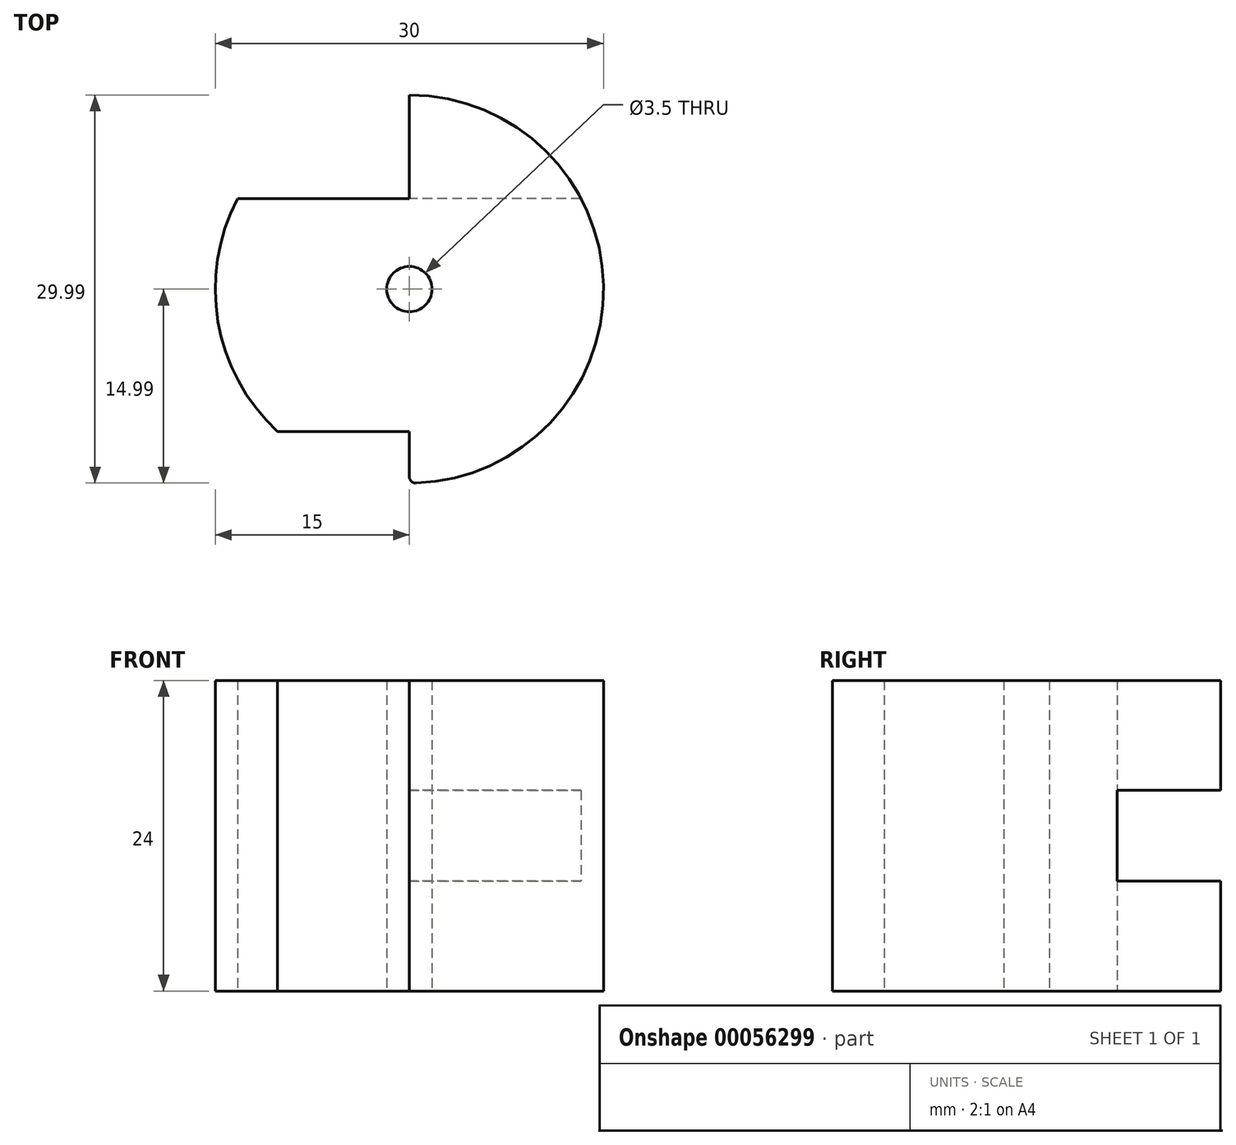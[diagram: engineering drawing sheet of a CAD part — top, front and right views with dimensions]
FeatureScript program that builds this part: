
annotation { "Feature Type Name" : "Feature", "Feature Type Description" : "" }
export const myFeature = defineFeature(function(context is Context, id is Id, definition is map)
    precondition{}
    {
        {
            var Q0;
            Q0=qCreatedBy(makeId("Top.planeOp"),FACE);
            var sketch = newSketch(context, id + "F0", { "sketchPlane" : qUnion([Q0])});
            skArc(sketch, "E0", {"start": v(-13.27, 7) * mm, "mid": v(-14.79, -2.52) * mm, "end": v(-10.2, -11) * mm});
            skLineSegment(sketch, "E1.bottom", {"start": v(-19.06, 20.86) * mm, "end": v(0, 20.86) * mm, "construction": true});
            skLineSegment(sketch, "E1.top", {"start": v(-19.06, 7) * mm, "end": v(-13.27, 7) * mm});
            skLineSegment(sketch, "E1.left", {"start": v(-19.06, 20.86) * mm, "end": v(-19.06, 7) * mm, "construction": true});
            skLineSegment(sketch, "E1.right", {"start": v(0, 20.86) * mm, "end": v(0, 7) * mm});
            skLineSegment(sketch, "E2.bottom", {"start": v(-16.2, -11) * mm, "end": v(-10.2, -11) * mm});
            skLineSegment(sketch, "E2.top", {"start": v(-16.2, -19.36) * mm, "end": v(0, -19.36) * mm, "construction": true});
            skLineSegment(sketch, "E2.left", {"start": v(-16.2, -11) * mm, "end": v(-16.2, -19.36) * mm, "construction": true});
            skLineSegment(sketch, "E2.right", {"start": v(0, -11) * mm, "end": v(0, -19.36) * mm});
            skLineSegment(sketch, "E3", {"start": v(0, 28.05) * mm, "end": v(0, 15) * mm, "construction": true});
            skCircle(sketch, "E4", {"center": v(0, 0) * mm, "radius": 1.75 * mm});
            skArc(sketch, "E5.trimOffspring", {"start": v(0, -15) * mm, "mid": v(15, 0) * mm, "end": v(0, 15) * mm});
            skLineSegment(sketch, "E6", {"start": v(0, 15) * mm, "end": v(0, -15) * mm, "construction": true});
            skLineSegment(sketch, "E7", {"start": v(-13.27, 7) * mm, "end": v(0, 7) * mm});
            skLineSegment(sketch, "E8", {"start": v(-10.2, -11) * mm, "end": v(0, -11) * mm});
            skLineSegment(sketch, "E9", {"start": v(0, -15) * mm, "end": v(0, -20.34) * mm, "construction": true});
            skSolve(sketch);
        }
        {
            var Q0;
            Q0=makeQuery(id+"F0.imprint","IMPRINT",FACE,{"disambiguationData":[TD([[makeQuery(id+"F0.imprint","IMPRINT",EDGE,{"derivedFrom":sQuery(id+"F0.wireOp",EDGE,"E0")}),1.0]])]});
            extrude(context, id + "F1", {"entities" : qUnion([Q0]), "depth" : 24 * mm});
        }
        {
            var Q0;
            Q0=makeQuery(id+"F1.opExtrude","SWEPT_EDGE",EDGE,{"disambiguationData":[OSD([sQuery(id+"F0.wireOp",EDGE,"E2.right"),sQuery(id+"F0.wireOp",EDGE,"E5.trimOffspring")])]});
            fillet(context, id + "F2", {"entities" : qUnion([Q0]), "radius" : 0.5 * mm, "tangentPropagation" : true, "allowEdgeOverflow" : false});
        }
        {
            var Q0;
            Q0=makeQuery(id+"F1.opExtrude","SWEPT_FACE",FACE,{"disambiguationData":[OSD([sQuery(id+"F0.wireOp",EDGE,"E1.right")])]});
            var sketch = newSketch(context, id + "F3", { "sketchPlane" : qUnion([Q0])});
            skLineSegment(sketch, "E10.0", {"start": v(-15, 24) * mm, "end": v(-15, 0) * mm, "construction": true});
            skLineSegment(sketch, "E11.0", {"start": v(-15, 24) * mm, "end": v(-7, 24) * mm, "construction": true});
            skLineSegment(sketch, "E12.0", {"start": v(-7, 24) * mm, "end": v(-7, 0) * mm, "construction": true});
            skLineSegment(sketch, "E13.0", {"start": v(-15, 0) * mm, "end": v(-7, 0) * mm, "construction": true});
            skLineSegment(sketch, "E14.bottom", {"start": v(-15, 8.5) * mm, "end": v(-7, 8.5) * mm});
            skLineSegment(sketch, "E14.top", {"start": v(-15, 15.5) * mm, "end": v(-7, 15.5) * mm});
            skLineSegment(sketch, "E14.left", {"start": v(-15, 8.5) * mm, "end": v(-15, 15.5) * mm});
            skLineSegment(sketch, "E14.right", {"start": v(-7, 8.5) * mm, "end": v(-7, 15.5) * mm});
            skLineSegment(sketch, "E15", {"start": v(-15, 12) * mm, "end": v(-7, 12) * mm, "construction": true});
            skSolve(sketch);
        }
        {
            var Q0;
            Q0=makeQuery(id+"F3.imprint","IMPRINT",FACE,{"disambiguationData":[TD([[makeQuery(id+"F3.imprint","IMPRINT",EDGE,{"derivedFrom":sQuery(id+"F3.wireOp",EDGE,"E14.bottom")}),1.0]])]});
            extrude(context, id + "F4", {"entities" : qUnion([Q0]), "operationType" : NewBodyOperationType.REMOVE, "endBound" : BoundingType.THROUGH_ALL, "oppositeDirection" : true, "depth" : 25 * mm});
        }
    });
